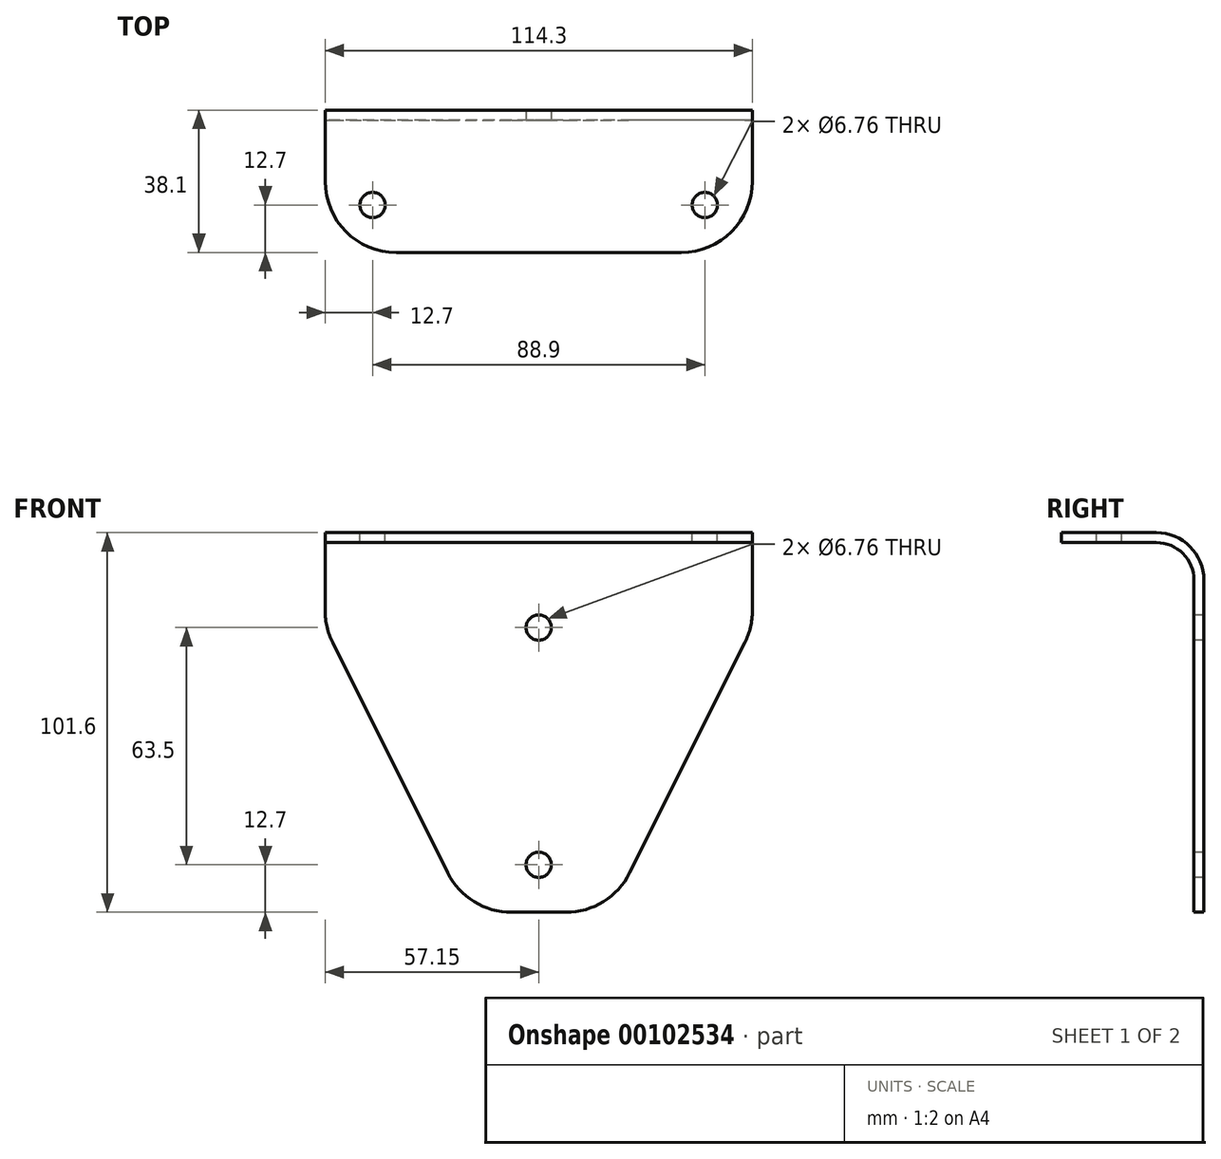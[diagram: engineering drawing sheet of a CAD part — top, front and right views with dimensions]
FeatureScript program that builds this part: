
annotation { "Feature Type Name" : "Feature", "Feature Type Description" : "" }
export const myFeature = defineFeature(function(context is Context, id is Id, definition is map)
    precondition{}
    {
        {
            var Q0;
            Q0=qCreatedBy(makeId("Top.planeOp"),FACE);
            var sketch = newSketch(context, id + "F0", { "sketchPlane" : qUnion([Q0])});
            skLineSegment(sketch, "E0.bottom", {"start": v(19.05, 19.05) * mm, "end": v(-19.05, 19.05) * mm, "construction": true});
            skLineSegment(sketch, "E0.top", {"start": v(19.05, -19.05) * mm, "end": v(-19.05, -19.05) * mm, "construction": true});
            skLineSegment(sketch, "E0.left", {"start": v(19.05, 19.05) * mm, "end": v(19.05, -19.05) * mm, "construction": true});
            skLineSegment(sketch, "E0.right", {"start": v(-19.05, 19.05) * mm, "end": v(-19.05, -19.05) * mm, "construction": true});
            skPoint(sketch, "E0.middle", {"position": v(0, 0) * mm});
            skSolve(sketch);
        }
        {
            var Q0;
            Q0=qCreatedBy(makeId("Front.planeOp"),FACE);
            cPlane(context, id + "F1", {"entities" : qUnion([Q0]), "cplaneType" : CPlaneType.OFFSET, "offset" : 19.05 * mm, "width" : 150 * mm, "height" : 150 * mm});
        }
        {
            var Q0;
            Q0=qCreatedBy(id+"F1.planeOp",FACE);
            var sketch = newSketch(context, id + "F2", { "sketchPlane" : qUnion([Q0])});
            skLineSegment(sketch, "E1", {"start": v(0, 0) * mm, "end": v(0, -45.36) * mm, "construction": true});
            skLineSegment(sketch, "E2", {"start": v(0, 0) * mm, "end": v(57.15, 0) * mm});
            skLineSegment(sketch, "E3", {"start": v(57.15, 0) * mm, "end": v(57.15, -25.4) * mm});
            skLineSegment(sketch, "E4", {"start": v(57.15, -25.4) * mm, "end": v(19.05, -101.6) * mm});
            skLineSegment(sketch, "E5", {"start": v(19.05, -101.6) * mm, "end": v(0, -101.6) * mm});
            skLineSegment(sketch, "E6.MirrorCS", {"start": v(0, 0) * mm, "end": v(-57.15, 0) * mm});
            skLineSegment(sketch, "E7.MirrorCS", {"start": v(-57.15, 0) * mm, "end": v(-57.15, -25.4) * mm});
            skLineSegment(sketch, "E8.MirrorCS", {"start": v(-57.15, -25.4) * mm, "end": v(-19.05, -101.6) * mm});
            skLineSegment(sketch, "E9.MirrorCS", {"start": v(-19.05, -101.6) * mm, "end": v(0, -101.6) * mm});
            skSolve(sketch);
        }
        {
            var Q0;
            Q0 = qSketchRegion(id + "F2", true);
            extrude(context, id + "F3", {"entities" : qUnion([Q0]), "depth" : 2.65 * mm});
        }
        {
            var Q0;
            Q0=makeQuery(id+"F3.opExtrude","SWEPT_FACE",FACE,{"disambiguationData":[OSD([sQuery(id+"F2.wireOp",EDGE,"E2"),sQuery(id+"F2.wireOp",EDGE,"E6.MirrorCS")])]});
            var sketch = newSketch(context, id + "F4", { "sketchPlane" : qUnion([Q0])});
            skLineSegment(sketch, "E10.bottom", {"start": v(-57.15, -19.05) * mm, "end": v(57.15, -19.05) * mm});
            skLineSegment(sketch, "E10.top", {"start": v(-57.15, -57.15) * mm, "end": v(57.15, -57.15) * mm});
            skLineSegment(sketch, "E10.left", {"start": v(-57.15, -19.05) * mm, "end": v(-57.15, -57.15) * mm});
            skLineSegment(sketch, "E10.right", {"start": v(57.15, -19.05) * mm, "end": v(57.15, -57.15) * mm});
            skSolve(sketch);
        }
        {
            var Q0;
            Q0 = qSketchRegion(id + "F4", true);
            extrude(context, id + "F5", {"entities" : qUnion([Q0]), "operationType" : NewBodyOperationType.ADD, "oppositeDirection" : true, "depth" : 2.65 * mm});
        }
        {
            var Q0;
            Q0=makeQuery(id+"F5.boolean.opBoolean","INTERSECT",EDGE,{"derivedFrom":[makeQuery(id+"F3.opExtrude","CAP_FACE",FACE,{"disambiguationData":[OSD([sQuery(id+"F2.wireOp",EDGE,"E2"),sQuery(id+"F2.wireOp",EDGE,"E3"),sQuery(id+"F2.wireOp",EDGE,"E4"),sQuery(id+"F2.wireOp",EDGE,"E5"),sQuery(id+"F2.wireOp",EDGE,"E6.MirrorCS"),sQuery(id+"F2.wireOp",EDGE,"E7.MirrorCS"),sQuery(id+"F2.wireOp",EDGE,"E8.MirrorCS"),sQuery(id+"F2.wireOp",EDGE,"E9.MirrorCS")])],"isStart":false}),makeQuery(id+"F5.opExtrude","CAP_FACE",FACE,{"disambiguationData":[OSD([sQuery(id+"F4.wireOp",EDGE,"E10.bottom"),sQuery(id+"F4.wireOp",EDGE,"E10.top"),sQuery(id+"F4.wireOp",EDGE,"E10.left"),sQuery(id+"F4.wireOp",EDGE,"E10.right")])],"isStart":false})]});
            fillet(context, id + "F6", {"entities" : qUnion([Q0]), "radius" : 10.05 * mm, "tangentPropagation" : true, "allowEdgeOverflow" : false});
        }
        {
            var Q0;
            Q0=makeQuery(id+"F3.opExtrude","CAP_EDGE",EDGE,{"disambiguationData":[OSD([sQuery(id+"F2.wireOp",EDGE,"E2"),sQuery(id+"F2.wireOp",EDGE,"E6.MirrorCS")])],"isStart":true});
            fillet(context, id + "F7", {"entities" : qUnion([Q0]), "radius" : 12.7 * mm, "tangentPropagation" : true, "allowEdgeOverflow" : false});
        }
        {
            var Q0;
            Q0=makeQuery(id+"F5.opExtrude","SWEPT_EDGE",EDGE,{"disambiguationData":[OSD([sQuery(id+"F4.wireOp",EDGE,"E10.top"),sQuery(id+"F4.wireOp",EDGE,"E10.left")])]});
            var Q1;
            Q1=makeQuery(id+"F5.opExtrude","SWEPT_EDGE",EDGE,{"disambiguationData":[OSD([sQuery(id+"F4.wireOp",EDGE,"E10.top"),sQuery(id+"F4.wireOp",EDGE,"E10.right")])]});
            var Q2;
            Q2=makeQuery(id+"F3.opExtrude","SWEPT_EDGE",EDGE,{"disambiguationData":[OSD([sQuery(id+"F2.wireOp",EDGE,"E7.MirrorCS"),sQuery(id+"F2.wireOp",EDGE,"E8.MirrorCS")])]});
            var Q3;
            Q3=makeQuery(id+"F3.opExtrude","SWEPT_EDGE",EDGE,{"disambiguationData":[OSD([sQuery(id+"F2.wireOp",EDGE,"E3"),sQuery(id+"F2.wireOp",EDGE,"E4")])]});
            var Q4;
            Q4=makeQuery(id+"F3.opExtrude","SWEPT_EDGE",EDGE,{"disambiguationData":[OSD([sQuery(id+"F2.wireOp",EDGE,"E4"),sQuery(id+"F2.wireOp",EDGE,"E5")])]});
            var Q5;
            Q5=makeQuery(id+"F3.opExtrude","SWEPT_EDGE",EDGE,{"disambiguationData":[OSD([sQuery(id+"F2.wireOp",EDGE,"E8.MirrorCS"),sQuery(id+"F2.wireOp",EDGE,"E9.MirrorCS")])]});
            fillet(context, id + "F8", {"entities" : qUnion([Q0, Q1, Q2, Q3, Q4, Q5]), "radius" : 19.05 * mm, "tangentPropagation" : true, "allowEdgeOverflow" : false});
        }
        {
            var Q0;
            Q0=makeQuery(id+"F5.boolean.opBoolean","MERGE",FACE,{"derivedFrom":[makeQuery(id+"F3.opExtrude","SWEPT_FACE",FACE,{"disambiguationData":[OSD([sQuery(id+"F2.wireOp",EDGE,"E2"),sQuery(id+"F2.wireOp",EDGE,"E6.MirrorCS")])]}),makeQuery(id+"F5.opExtrude","CAP_FACE",FACE,{"disambiguationData":[OSD([sQuery(id+"F4.wireOp",EDGE,"E10.bottom"),sQuery(id+"F4.wireOp",EDGE,"E10.top"),sQuery(id+"F4.wireOp",EDGE,"E10.left"),sQuery(id+"F4.wireOp",EDGE,"E10.right")])],"isStart":true})]});
            var sketch = newSketch(context, id + "F9", { "sketchPlane" : qUnion([Q0])});
            skLineSegment(sketch, "E11", {"start": v(0, 0) * mm, "end": v(0, -41.5) * mm, "construction": true});
            skPoint(sketch, "E12", {"position": v(44.45, -44.45) * mm});
            skPoint(sketch, "E13.MirrorP", {"position": v(-44.45, -44.45) * mm});
            skSolve(sketch);
        }
        {
            var Q0;
            Q0=sQuery(id+"F9.wireOp",VERTEX,"E13.MirrorP");
            var Q1;
            Q1=sQuery(id+"F9.wireOp",VERTEX,"E12");
            var Q2;
            Q2=makeQuery(id+"F3.opExtrude","SWEPT_BODY",BODY,{"disambiguationData":[OSD([sQuery(id+"F2.wireOp",EDGE,"E2"),sQuery(id+"F2.wireOp",EDGE,"E3"),sQuery(id+"F2.wireOp",EDGE,"E4"),sQuery(id+"F2.wireOp",EDGE,"E5"),sQuery(id+"F2.wireOp",EDGE,"E6.MirrorCS"),sQuery(id+"F2.wireOp",EDGE,"E7.MirrorCS"),sQuery(id+"F2.wireOp",EDGE,"E8.MirrorCS"),sQuery(id+"F2.wireOp",EDGE,"E9.MirrorCS")])]});
            hole(context, id + "F10", {"style" : HoleStyle.SIMPLE, "endStyle" : HoleEndStyle.THROUGH, "standardTappedOrClearance" : lookupTablePath({ "standard" : "ANSI", "fit" : "Normal (ASME)", "size" : "1/4", "type" : "Clearance" }), "standardBlindInLast" : lookupTablePath({ "fit" : "Free", "standard" : "ANSI", "size" : "1/4", "type" : "Clearance" }), "holeDiameter" : 6.76 * mm, "locations" : qUnion([Q0, Q1]), "scope" : qUnion([Q2]), "isTappedThrough" : true});
        }
        {
            var Q0;
            Q0=makeQuery(id+"F3.opExtrude","CAP_FACE",FACE,{"disambiguationData":[OSD([sQuery(id+"F2.wireOp",EDGE,"E2"),sQuery(id+"F2.wireOp",EDGE,"E3"),sQuery(id+"F2.wireOp",EDGE,"E4"),sQuery(id+"F2.wireOp",EDGE,"E5"),sQuery(id+"F2.wireOp",EDGE,"E6.MirrorCS"),sQuery(id+"F2.wireOp",EDGE,"E7.MirrorCS"),sQuery(id+"F2.wireOp",EDGE,"E8.MirrorCS"),sQuery(id+"F2.wireOp",EDGE,"E9.MirrorCS")])],"isStart":false});
            var sketch = newSketch(context, id + "F11", { "sketchPlane" : qUnion([Q0])});
            skLineSegment(sketch, "E14", {"start": v(0, -57.15) * mm, "end": v(22.02, -57.15) * mm, "construction": true});
            skPoint(sketch, "E15", {"position": v(0, -25.4) * mm});
            skPoint(sketch, "E16.MirrorP", {"position": v(0, -88.9) * mm});
            skSolve(sketch);
        }
        {
            var Q0;
            Q0=sQuery(id+"F11.wireOp",VERTEX,"E15");
            var Q1;
            Q1=sQuery(id+"F11.wireOp",VERTEX,"E16.MirrorP");
            var Q2;
            Q2=makeQuery(id+"F3.opExtrude","SWEPT_BODY",BODY,{"disambiguationData":[OSD([sQuery(id+"F2.wireOp",EDGE,"E2"),sQuery(id+"F2.wireOp",EDGE,"E3"),sQuery(id+"F2.wireOp",EDGE,"E4"),sQuery(id+"F2.wireOp",EDGE,"E5"),sQuery(id+"F2.wireOp",EDGE,"E6.MirrorCS"),sQuery(id+"F2.wireOp",EDGE,"E7.MirrorCS"),sQuery(id+"F2.wireOp",EDGE,"E8.MirrorCS"),sQuery(id+"F2.wireOp",EDGE,"E9.MirrorCS")])]});
            hole(context, id + "F12", {"style" : HoleStyle.SIMPLE, "endStyle" : HoleEndStyle.THROUGH, "standardTappedOrClearance" : lookupTablePath({ "standard" : "ANSI", "fit" : "Normal (ASME)", "size" : "1/4", "type" : "Clearance" }), "standardBlindInLast" : lookupTablePath({ "fit" : "Free", "standard" : "ANSI", "size" : "1/4", "type" : "Clearance" }), "holeDiameter" : 6.76 * mm, "locations" : qUnion([Q0, Q1]), "scope" : qUnion([Q2]), "isTappedThrough" : true});
        }
    });
